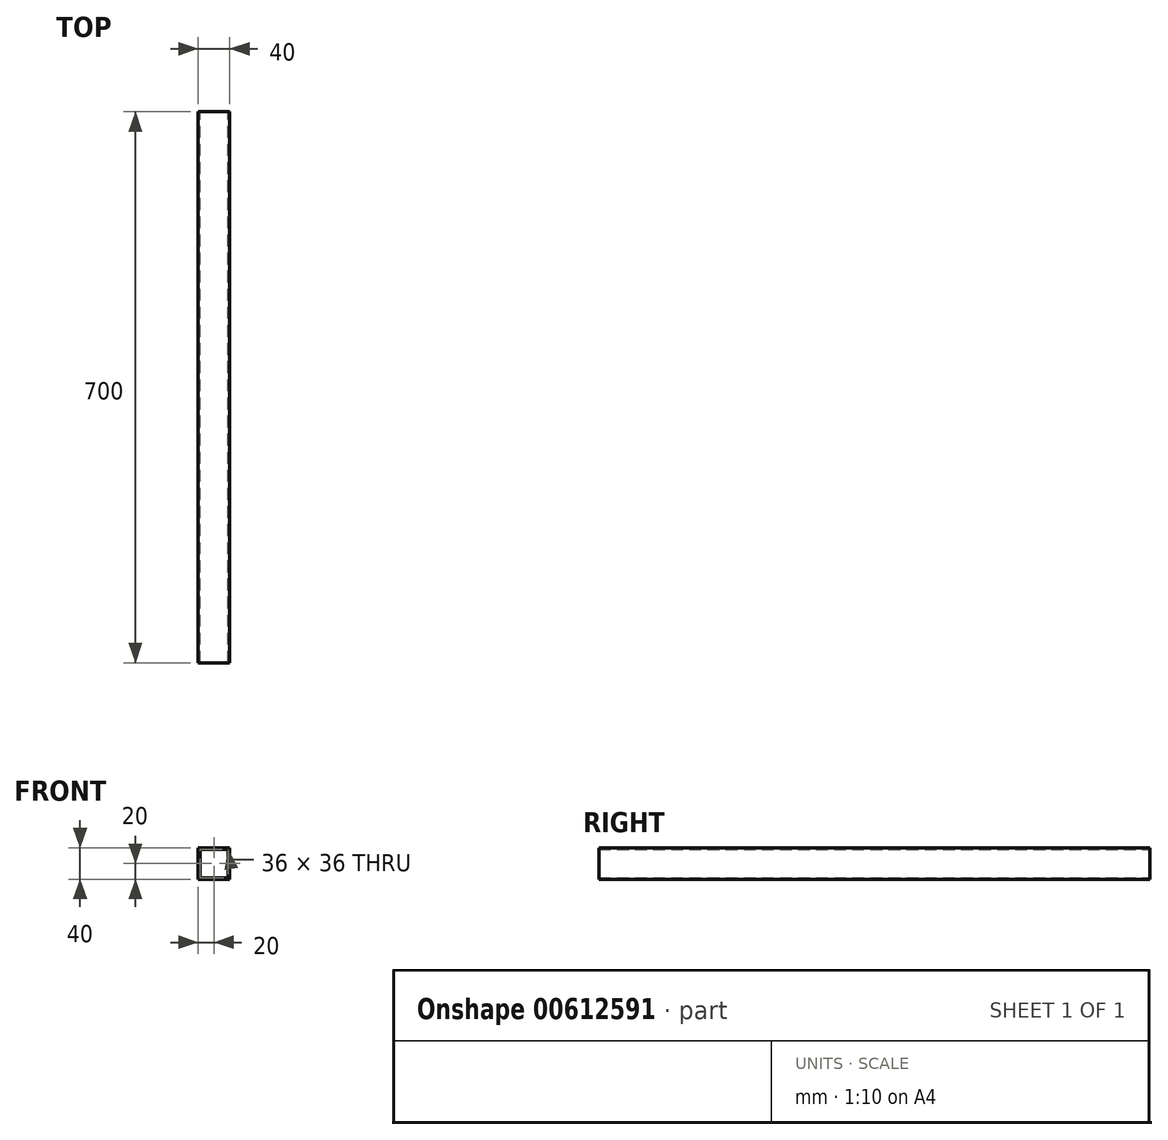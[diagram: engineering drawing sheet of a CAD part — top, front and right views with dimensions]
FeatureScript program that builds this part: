
annotation { "Feature Type Name" : "Feature", "Feature Type Description" : "" }
export const myFeature = defineFeature(function(context is Context, id is Id, definition is map)
    precondition{}
    {
        {
            var Q0;
            Q0=qCreatedBy(makeId("Front.planeOp"),FACE);
            var sketch = newSketch(context, id + "F0", { "sketchPlane" : qUnion([Q0])});
            skLineSegment(sketch, "E0.bottom", {"start": v(0, 0) * mm, "end": v(40, 0) * mm});
            skLineSegment(sketch, "E0.top", {"start": v(0, -40) * mm, "end": v(40, -40) * mm});
            skLineSegment(sketch, "E0.left", {"start": v(0, 0) * mm, "end": v(0, -40) * mm});
            skLineSegment(sketch, "E0.right", {"start": v(40, 0) * mm, "end": v(40, -40) * mm});
            skLineSegment(sketch, "E1.0", {"start": v(2, -2) * mm, "end": v(38, -2) * mm});
            skLineSegment(sketch, "E1.1", {"start": v(2, -2) * mm, "end": v(2, -38) * mm});
            skLineSegment(sketch, "E1.2", {"start": v(2, -38) * mm, "end": v(38, -38) * mm});
            skLineSegment(sketch, "E1.3", {"start": v(38, -2) * mm, "end": v(38, -38) * mm});
            skSolve(sketch);
        }
        {
            var Q0;
            Q0=makeQuery(id+"F0.imprint","IMPRINT",FACE,{"disambiguationData":[TD([[makeQuery(id+"F0.imprint","IMPRINT",EDGE,{"derivedFrom":sQuery(id+"F0.wireOp",EDGE,"E0.bottom")}),-1.0]])]});
            extrude(context, id + "F1", {"entities" : qUnion([Q0]), "depth" : 700 * mm, "offsetDistance" : 25.4 * mm});
        }
    });
